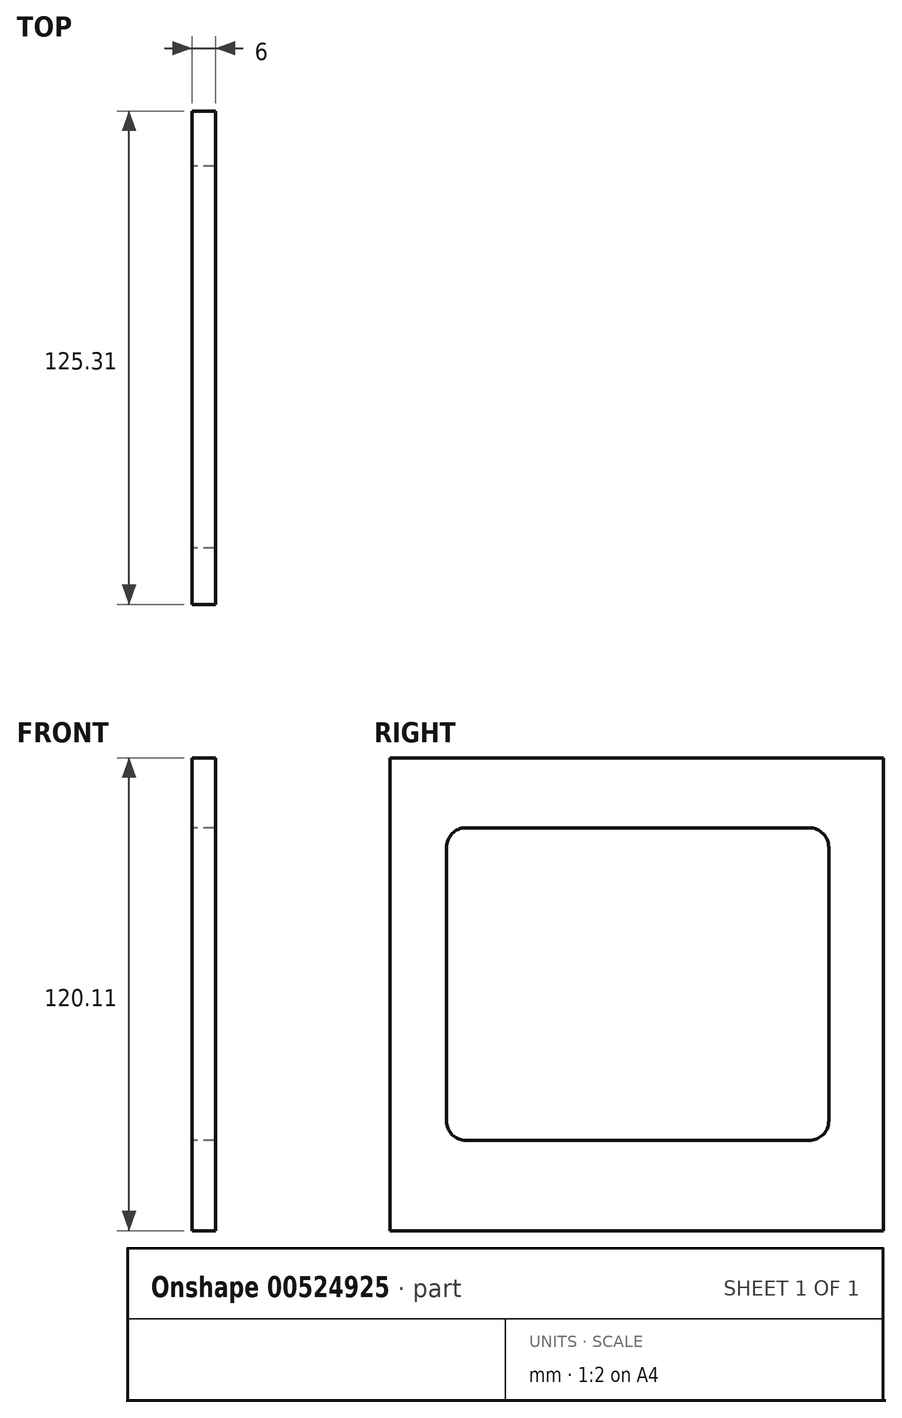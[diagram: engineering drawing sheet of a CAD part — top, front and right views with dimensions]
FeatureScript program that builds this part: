
annotation { "Feature Type Name" : "Feature", "Feature Type Description" : "" }
export const myFeature = defineFeature(function(context is Context, id is Id, definition is map)
    precondition{}
    {
        {
            var Q0;
            Q0=qCreatedBy(makeId("Right.planeOp"),FACE);
            var sketch = newSketch(context, id + "F0", { "sketchPlane" : qUnion([Q0])});
            skLineSegment(sketch, "E0.bottom", {"start": v(-64.84, 60.6) * mm, "end": v(60.47, 60.6) * mm});
            skLineSegment(sketch, "E0.top", {"start": v(-64.84, -59.51) * mm, "end": v(60.47, -59.51) * mm});
            skLineSegment(sketch, "E0.left", {"start": v(-64.84, 60.6) * mm, "end": v(-64.84, -59.51) * mm});
            skLineSegment(sketch, "E0.right", {"start": v(60.47, 60.6) * mm, "end": v(60.47, -59.51) * mm});
            skLineSegment(sketch, "E1.bottom", {"start": v(-45.56, 42.84) * mm, "end": v(41.57, 42.84) * mm});
            skLineSegment(sketch, "E1.top", {"start": v(-45.56, -36.6) * mm, "end": v(41.57, -36.6) * mm});
            skLineSegment(sketch, "E1.left", {"start": v(-50.56, 37.84) * mm, "end": v(-50.56, -31.6) * mm});
            skLineSegment(sketch, "E1.right", {"start": v(46.57, 37.84) * mm, "end": v(46.57, -31.6) * mm});
            skPoint(sketch, "E2.visualSharp", {"position": v(-50.56, 42.84) * mm});
            skArc(sketch, "E2.filletArc", {"start": v(-45.56, 42.84) * mm, "mid": v(-49.1, 41.38) * mm, "end": v(-50.56, 37.84) * mm});
            skPoint(sketch, "E3.visualSharp", {"position": v(46.57, 42.84) * mm});
            skArc(sketch, "E3.filletArc", {"start": v(46.57, 37.84) * mm, "mid": v(45.1, 41.38) * mm, "end": v(41.57, 42.84) * mm});
            skPoint(sketch, "E4.visualSharp", {"position": v(-50.56, -36.6) * mm});
            skArc(sketch, "E4.filletArc", {"start": v(-50.56, -31.6) * mm, "mid": v(-49.1, -35.14) * mm, "end": v(-45.56, -36.6) * mm});
            skPoint(sketch, "E5.visualSharp", {"position": v(46.57, -36.6) * mm});
            skArc(sketch, "E5.filletArc", {"start": v(41.57, -36.6) * mm, "mid": v(45.1, -35.14) * mm, "end": v(46.57, -31.6) * mm});
            skSolve(sketch);
        }
        {
            var Q0;
            Q0=makeQuery(id+"F0.imprint","IMPRINT",FACE,{"disambiguationData":[TD([[makeQuery(id+"F0.imprint","IMPRINT",EDGE,{"derivedFrom":sQuery(id+"F0.wireOp",EDGE,"E0.bottom")}),-1.0]])]});
            extrude(context, id + "F1", {"entities" : qUnion([Q0]), "depth" : 6 * mm, "offsetDistance" : 25 * mm});
        }
    });
